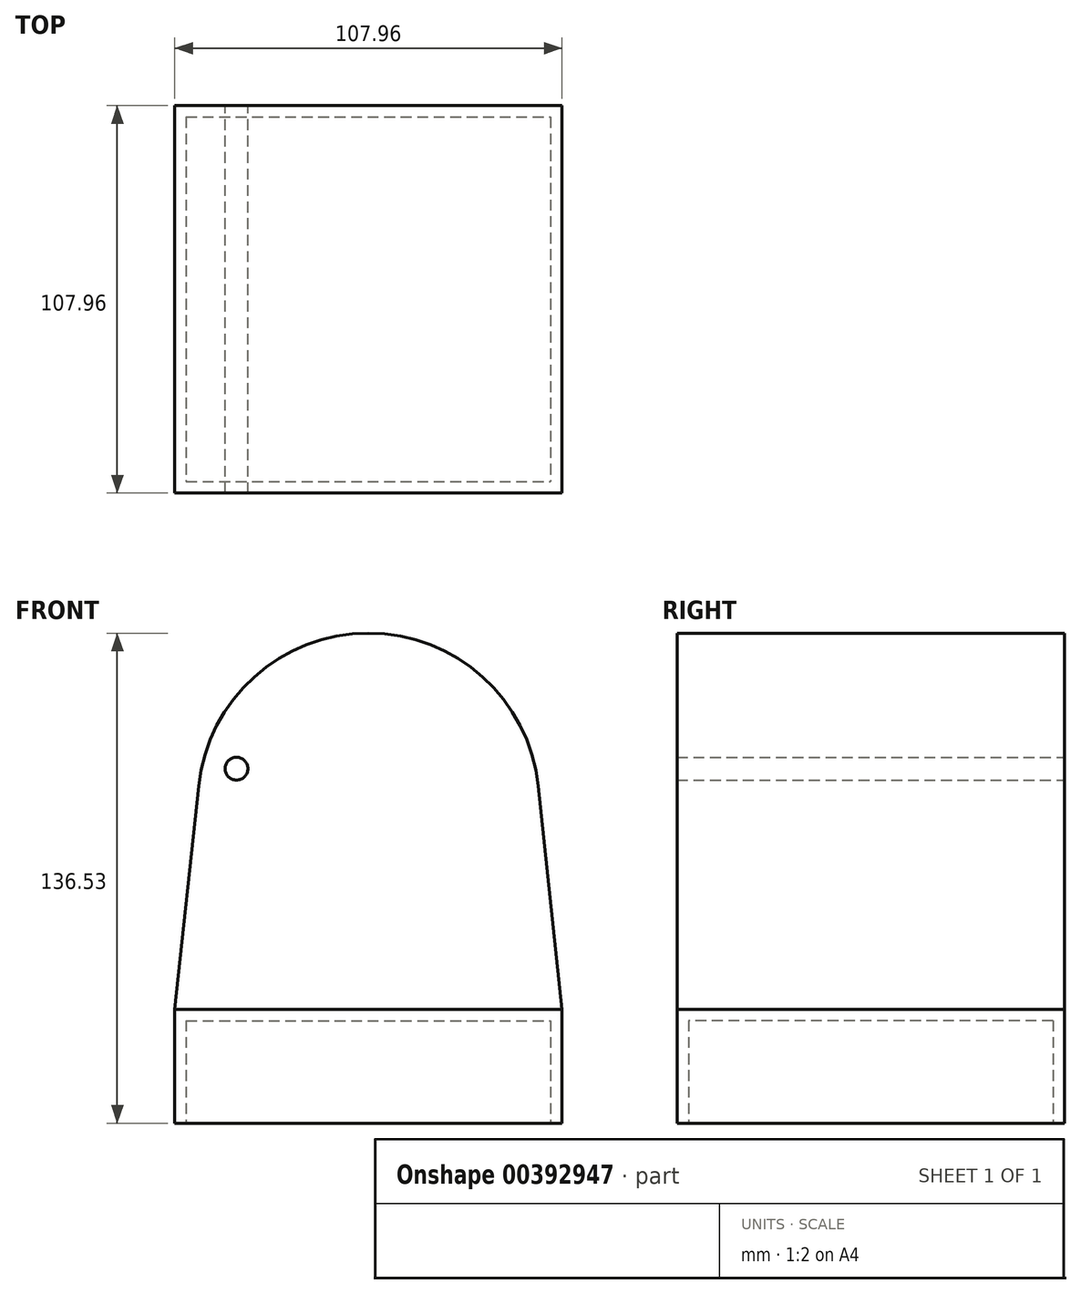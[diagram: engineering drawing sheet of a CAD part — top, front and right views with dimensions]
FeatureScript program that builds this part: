
annotation { "Feature Type Name" : "Feature", "Feature Type Description" : "" }
export const myFeature = defineFeature(function(context is Context, id is Id, definition is map)
    precondition{}
    {
        {
            var Q0;
            Q0=qCreatedBy(makeId("Top.planeOp"),FACE);
            var sketch = newSketch(context, id + "F0", { "sketchPlane" : qUnion([Q0])});
            skLineSegment(sketch, "E0.bottom", {"start": v(53.97, 53.98) * mm, "end": v(-53.98, 53.98) * mm});
            skLineSegment(sketch, "E0.top", {"start": v(53.98, -53.98) * mm, "end": v(-53.97, -53.98) * mm});
            skLineSegment(sketch, "E0.left", {"start": v(53.97, 53.97) * mm, "end": v(53.98, -53.98) * mm});
            skLineSegment(sketch, "E0.right", {"start": v(-53.98, 53.97) * mm, "end": v(-53.97, -53.98) * mm});
            skPoint(sketch, "E0.middle", {"position": v(0, 0) * mm});
            skSolve(sketch);
        }
        {
            var Q0;
            Q0=makeQuery(id+"F0.imprint","IMPRINT",FACE,{"disambiguationData":[TD([[makeQuery(id+"F0.imprint","IMPRINT",EDGE,{"derivedFrom":sQuery(id+"F0.wireOp",EDGE,"E0.bottom")}),1.0]])]});
            extrude(context, id + "F1", {"entities" : qUnion([Q0]), "depth" : 31.75 * mm});
        }
        {
            var Q0;
            Q0=makeQuery(id+"F1.opExtrude","CAP_FACE",FACE,{"disambiguationData":[OSD([sQuery(id+"F0.wireOp",EDGE,"E0.bottom"),sQuery(id+"F0.wireOp",EDGE,"E0.top"),sQuery(id+"F0.wireOp",EDGE,"E0.left"),sQuery(id+"F0.wireOp",EDGE,"E0.right")])],"isStart":true});
            var sketch = newSketch(context, id + "F2", { "sketchPlane" : qUnion([Q0])});
            skLineSegment(sketch, "E1.bottom", {"start": v(-50.8, -50.8) * mm, "end": v(50.8, -50.8) * mm});
            skLineSegment(sketch, "E1.top", {"start": v(-50.8, 50.8) * mm, "end": v(50.8, 50.8) * mm});
            skLineSegment(sketch, "E1.left", {"start": v(-50.8, -50.8) * mm, "end": v(-50.8, 50.8) * mm});
            skLineSegment(sketch, "E1.right", {"start": v(50.8, -50.8) * mm, "end": v(50.8, 50.8) * mm});
            skPoint(sketch, "E1.middle", {"position": v(0, 0) * mm});
            skSolve(sketch);
        }
        {
            var Q0;
            Q0 = qSketchRegion(id + "F2", true);
            extrude(context, id + "F3", {"entities" : qUnion([Q0]), "operationType" : NewBodyOperationType.REMOVE, "oppositeDirection" : true, "depth" : 28.57 * mm});
        }
        {
            var Q0;
            Q0=qCreatedBy(makeId("Front.planeOp"),FACE);
            var sketch = newSketch(context, id + "F4", { "sketchPlane" : qUnion([Q0])});
            skArc(sketch, "E2", {"start": v(47.36, 93.94) * mm, "mid": v(0, 136.53) * mm, "end": v(-47.36, 93.94) * mm});
            skLineSegment(sketch, "E3", {"start": v(-47.36, 93.94) * mm, "end": v(-53.98, 31.75) * mm});
            skLineSegment(sketch, "E4", {"start": v(-53.98, 31.75) * mm, "end": v(53.97, 31.75) * mm});
            skLineSegment(sketch, "E5", {"start": v(53.97, 31.75) * mm, "end": v(47.36, 93.94) * mm});
            skSolve(sketch);
        }
        {
            var Q0;
            Q0=makeQuery(id+"F4.imprint","IMPRINT",FACE,{"disambiguationData":[TD([[makeQuery(id+"F4.imprint","IMPRINT",EDGE,{"derivedFrom":sQuery(id+"F4.wireOp",EDGE,"E2")}),1.0]])]});
            extrude(context, id + "F5", {"entities" : qUnion([Q0]), "depth" : 107.95 * mm, "symmetric" : true});
        }
        {
            var Q0;
            Q0=makeQuery(id+"F5.opExtrude","CAP_FACE",FACE,{"disambiguationData":[OSD([sQuery(id+"F4.wireOp",EDGE,"E2"),sQuery(id+"F4.wireOp",EDGE,"E3"),sQuery(id+"F4.wireOp",EDGE,"E4"),sQuery(id+"F4.wireOp",EDGE,"E5")])],"isStart":false});
            var sketch = newSketch(context, id + "F6", { "sketchPlane" : qUnion([Q0])});
            skCircle(sketch, "E6", {"center": v(-36.8, 98.76) * mm, "radius": 3.18 * mm});
            skLineSegment(sketch, "E7", {"start": v(-36.8, 98.76) * mm, "end": v(0, 88.9) * mm, "construction": true});
            skLineSegment(sketch, "E8", {"start": v(0, 88.9) * mm, "end": v(-38.1, 88.9) * mm, "construction": true});
            skSolve(sketch);
        }
        {
            var Q0;
            Q0=sQuery(id+"F6.wireOp",VERTEX,"E7.start");
            var Q1;
            Q1=makeQuery(id+"F5.opExtrude","SWEPT_BODY",BODY,{"disambiguationData":[OSD([sQuery(id+"F4.wireOp",EDGE,"E2"),sQuery(id+"F4.wireOp",EDGE,"E3"),sQuery(id+"F4.wireOp",EDGE,"E4"),sQuery(id+"F4.wireOp",EDGE,"E5")])]});
            hole(context, id + "F7", {"style" : HoleStyle.SIMPLE, "endStyle" : HoleEndStyle.THROUGH, "holeDiameter" : 6.35 * mm, "majorDiameter" : 6.35 * mm, "isTappedThrough" : true, "tappedDepth" : 12.7 * mm, "tapClearance" : 3, "locations" : qUnion([Q0]), "scope" : qUnion([Q1]), "startStyle" : HoleStartStyle.PART});
        }
    });
